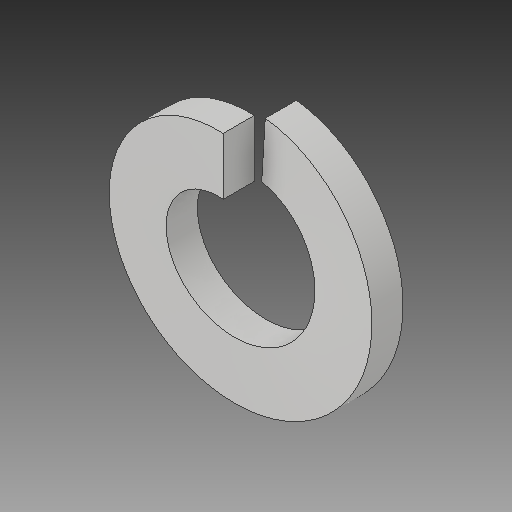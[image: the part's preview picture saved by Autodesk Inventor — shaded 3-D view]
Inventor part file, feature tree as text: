
AUTODESK INVENTOR PART (.ipt)
format: ipt  version: 2018 (Build 220112000, 112)  size: 139,264 bytes
history: native  units: in
note: dims shown in document units (in); Inventor stores cm internally (conversion verified against a paired STEP export)
features: sweep x1
ambient origin geometry x8: Origin, YZ Plane, XZ Plane, XY Plane, X Axis, Y Axis, Z Axis, Center Point
bodies: Solid1 (feature_tree)
feature tree (1):
  sweep  "Sweep1"
